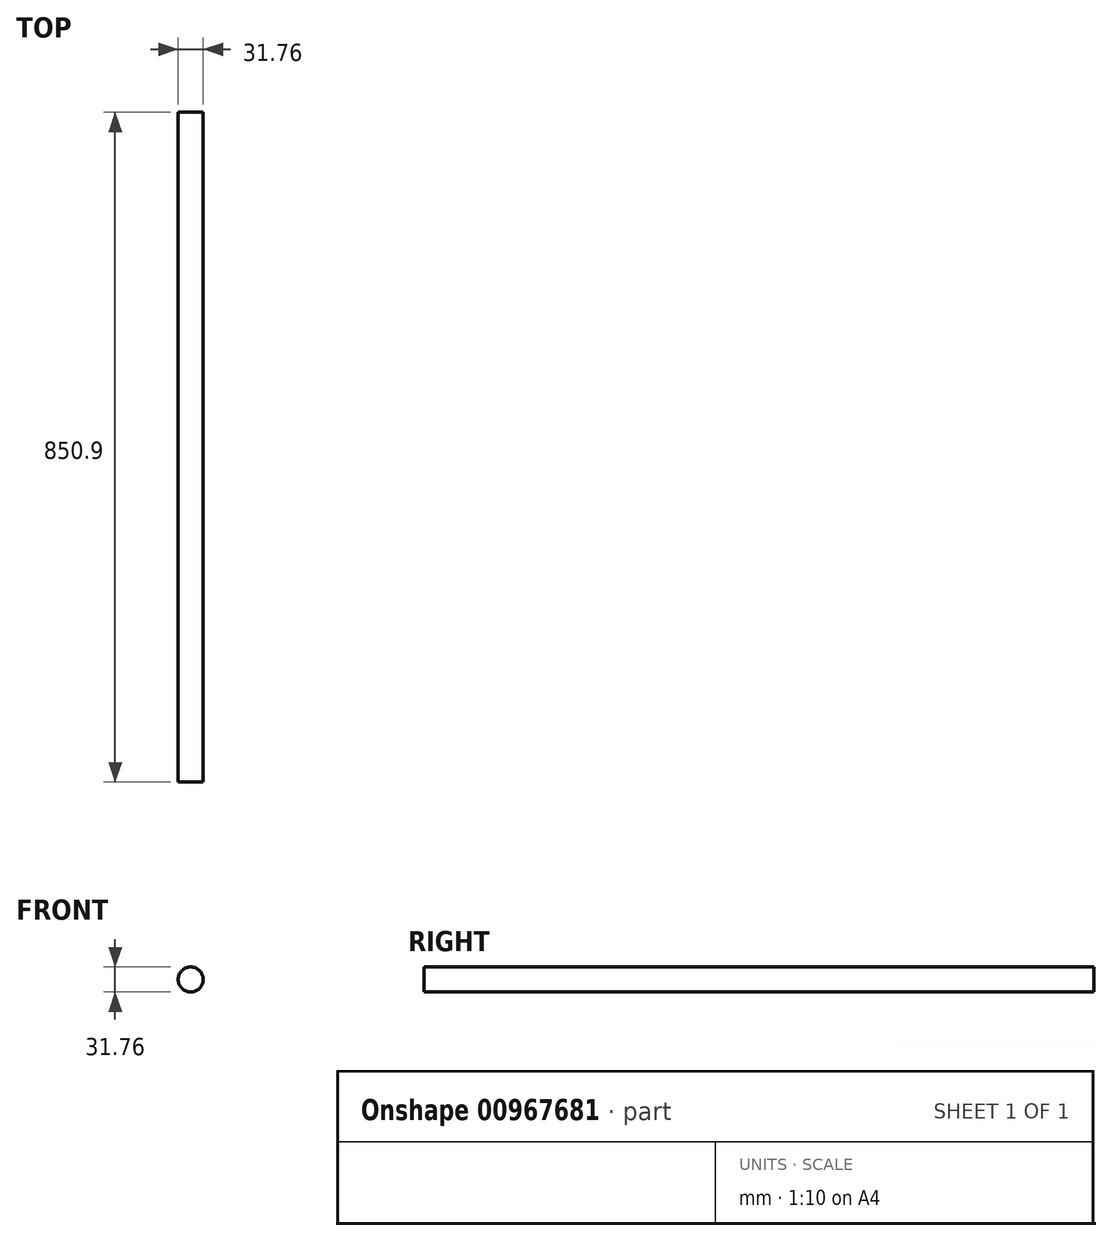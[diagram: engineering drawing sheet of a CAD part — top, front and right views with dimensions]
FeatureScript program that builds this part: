
annotation { "Feature Type Name" : "Feature", "Feature Type Description" : "" }
export const myFeature = defineFeature(function(context is Context, id is Id, definition is map)
    precondition{}
    {
        {
            var Q0;
            Q0=qCreatedBy(makeId("Front.planeOp"),FACE);
            var sketch = newSketch(context, id + "F0", { "sketchPlane" : qUnion([Q0])});
            skCircle(sketch, "E0", {"center": v(0, 0) * mm, "radius": 15.88 * mm});
            skSolve(sketch);
        }
        {
            var Q0;
            Q0 = qSketchRegion(id + "F0", true);
            extrude(context, id + "F1", {"entities" : qUnion([Q0]), "depth" : 850.9 * mm, "offsetDistance" : 25.4 * mm});
        }
    });
